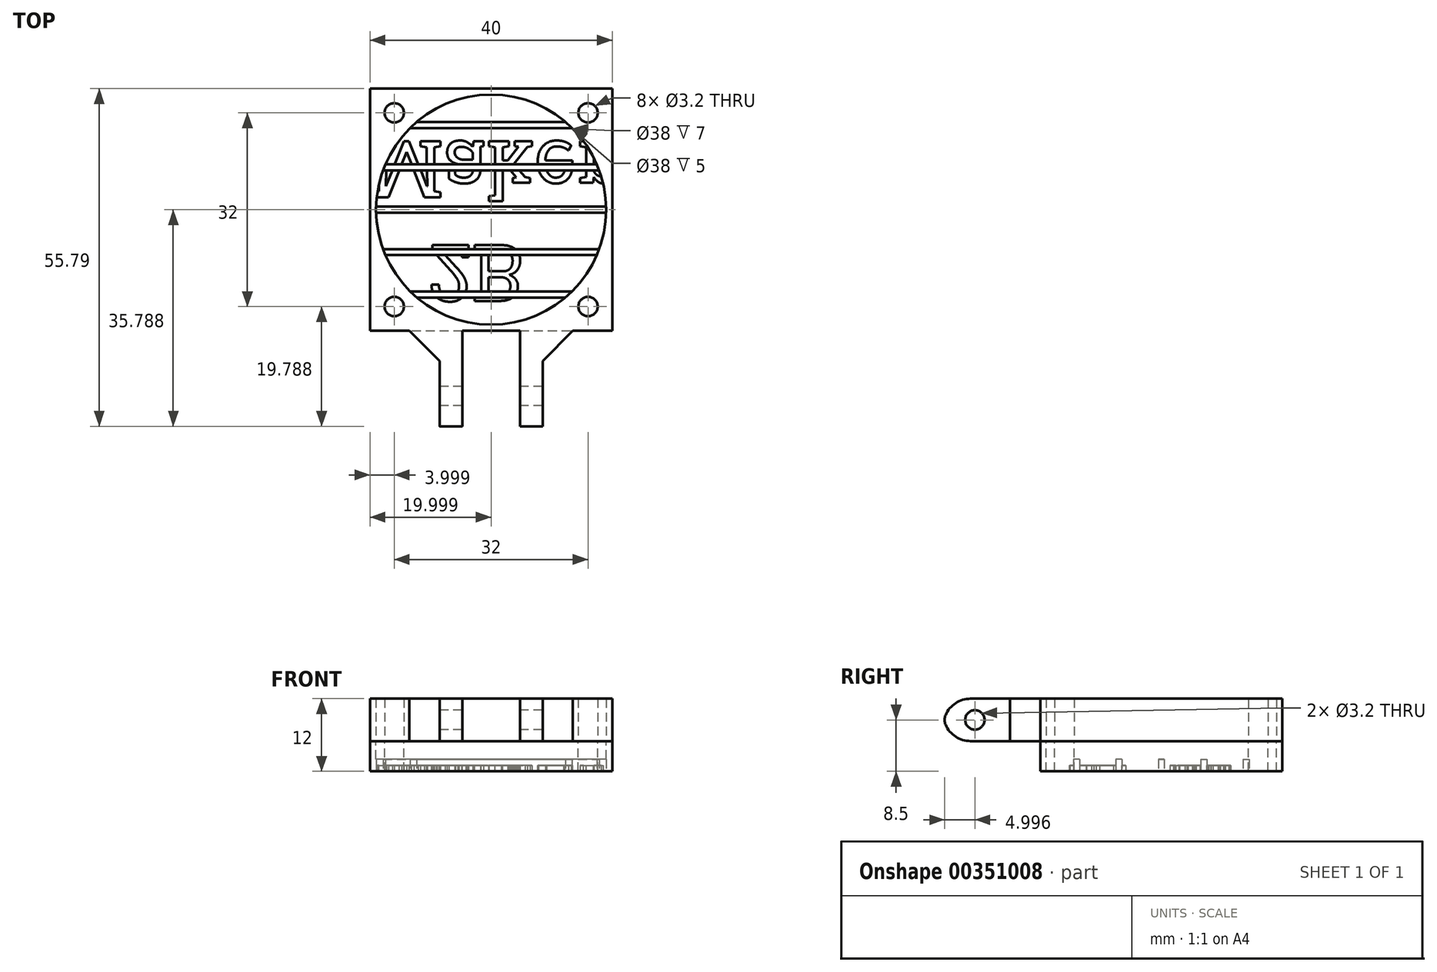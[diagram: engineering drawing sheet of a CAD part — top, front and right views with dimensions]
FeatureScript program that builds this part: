
annotation { "Feature Type Name" : "Feature", "Feature Type Description" : "" }
export const myFeature = defineFeature(function(context is Context, id is Id, definition is map)
    precondition{}
    {
        {
            var Q0;
            Q0=qCreatedBy(makeId("Top.planeOp"),FACE);
            var sketch = newSketch(context, id + "F0", { "sketchPlane" : qUnion([Q0])});
            skLineSegment(sketch, "E0.bottom", {"start": v(-56.17, -10.13) * mm, "end": v(-16.17, -10.13) * mm});
            skLineSegment(sketch, "E0.top", {"start": v(-56.17, 29.87) * mm, "end": v(-16.17, 29.87) * mm});
            skLineSegment(sketch, "E0.left", {"start": v(-56.17, -10.13) * mm, "end": v(-56.17, 29.87) * mm});
            skLineSegment(sketch, "E0.right", {"start": v(-16.17, -10.13) * mm, "end": v(-16.17, 29.87) * mm});
            skLineSegment(sketch, "E1.bottom", {"start": v(-55.17, 28.87) * mm, "end": v(-17.17, 28.87) * mm});
            skLineSegment(sketch, "E1.top", {"start": v(-55.17, -9.13) * mm, "end": v(-17.17, -9.13) * mm});
            skLineSegment(sketch, "E1.left", {"start": v(-55.17, 28.87) * mm, "end": v(-55.17, -9.13) * mm});
            skLineSegment(sketch, "E1.right", {"start": v(-17.17, 28.87) * mm, "end": v(-17.17, -9.13) * mm});
            skCircle(sketch, "E2", {"center": v(-52.17, 25.87) * mm, "radius": 1.6 * mm});
            skCircle(sketch, "E3", {"center": v(-52.17, -6.13) * mm, "radius": 1.6 * mm});
            skCircle(sketch, "E4", {"center": v(-20.17, -6.13) * mm, "radius": 1.6 * mm});
            skCircle(sketch, "E5", {"center": v(-20.17, 25.87) * mm, "radius": 1.6 * mm});
            skLineSegment(sketch, "E6", {"start": v(-56.17, 29.87) * mm, "end": v(-36.17, 29.87) * mm});
            skCircle(sketch, "E7", {"center": v(-36.17, 9.87) * mm, "radius": 19 * mm});
            skCircle(sketch, "E8", {"center": v(-36.17, 9.87) * mm, "radius": 18.03 * mm});
            skLineSegment(sketch, "E9", {"start": v(-52.3, 1.82) * mm, "end": v(-53.06, 1.15) * mm});
            skPoint(sketch, "E10.endSnap0", {"position": v(-36.17, -9.13) * mm});
            skLineSegment(sketch, "E11", {"start": v(-36.17, -10.1) * mm, "end": v(-31.82, -10.1) * mm});
            skLineSegment(sketch, "E12", {"start": v(-31.82, -10.1) * mm, "end": v(-28.07, -10.1) * mm});
            skLineSegment(sketch, "E13", {"start": v(-36.17, -10.1) * mm, "end": v(-40.52, -10.1) * mm});
            skLineSegment(sketch, "E14", {"start": v(-40.52, -10.1) * mm, "end": v(-44.27, -10.1) * mm});
            skSolve(sketch);
        }
        {
            var Q0;
            Q0 = qSketchRegion(id + "F0", true);
            var Q1;
            Q1=makeQuery(id+"F0.imprint","IMPRINT",FACE,{"disambiguationData":[TD([[makeQuery(id+"F0.imprint","IMPRINT",EDGE,{"derivedFrom":sQuery(id+"F0.wireOp",EDGE,"E2")}),-1.0]])]});
            var Q2;
            Q2=makeQuery(id+"F0.imprint","IMPRINT",FACE,{"disambiguationData":[TD([[makeQuery(id+"F0.imprint","IMPRINT",EDGE,{"derivedFrom":sQuery(id+"F0.wireOp",EDGE,"E5")}),-1.0]])]});
            var Q3;
            Q3=makeQuery(id+"F0.imprint","IMPRINT",FACE,{"disambiguationData":[TD([[makeQuery(id+"F0.imprint","IMPRINT",EDGE,{"derivedFrom":sQuery(id+"F0.wireOp",EDGE,"E3")}),-1.0]])]});
            var Q4;
            Q4=makeQuery(id+"F0.imprint","IMPRINT",FACE,{"disambiguationData":[TD([[makeQuery(id+"F0.imprint","IMPRINT",EDGE,{"derivedFrom":sQuery(id+"F0.wireOp",EDGE,"E4")}),-1.0]])]});
            extrude(context, id + "F1", {"entities" : qUnion([Q0, Q1, Q2, Q3, Q4]), "depth" : 7 * mm});
        }
        {
            var Q0;
            Q0=makeQuery(id+"F1.opExtrude","SWEPT_FACE",FACE,{"disambiguationData":[OSD([sQuery(id+"F0.wireOp",EDGE,"E0.bottom")])]});
            var sketch = newSketch(context, id + "F2", { "sketchPlane" : qUnion([Q0])});
            skLineSegment(sketch, "E15", {"start": v(-36.17, 0) * mm, "end": v(-36.17, 7) * mm});
            skLineSegment(sketch, "E16", {"start": v(-44.67, 7) * mm, "end": v(-44.67, 0) * mm});
            skLineSegment(sketch, "E17", {"start": v(-40.92, 7) * mm, "end": v(-40.92, 0) * mm});
            skLineSegment(sketch, "E18", {"start": v(-31.42, 0) * mm, "end": v(-31.42, 7) * mm});
            skLineSegment(sketch, "E19", {"start": v(-27.67, 0) * mm, "end": v(-27.67, 7) * mm});
            skSolve(sketch);
        }
        {
            var Q0;
            {var subQ0=sQuery(id+"F2.wireOp",EDGE,"E16");Q0=makeQuery(id+"F2.imprint","IMPRINT",FACE,{"disambiguationData":[TD([[makeQuery(id+"F2.imprint","IMPRINT",EDGE,{"derivedFrom":subQ0}),1.0]])]});}
            var Q1;
            {var subQ0=sQuery(id+"F2.wireOp",EDGE,"E18");Q1=makeQuery(id+"F2.imprint","IMPRINT",FACE,{"disambiguationData":[TD([[makeQuery(id+"F2.imprint","IMPRINT",EDGE,{"derivedFrom":subQ0}),-1.0]])]});}
            extrude(context, id + "F3", {"entities" : qUnion([Q0, Q1]), "operationType" : NewBodyOperationType.ADD, "depth" : 16 * mm});
        }
        {
            var Q0;
            {var subQ0=sQuery(id+"F0.wireOp",EDGE,"E0.bottom");var subQ1=makeQuery(id+"F1.opExtrude","CAP_EDGE",EDGE,{"disambiguationData":[OSD([subQ0])],"isStart":false});Q0=makeQuery(id+"F3.opExtrude","CAP_EDGE",EDGE,{"disambiguationData":[OSD([subQ0]),TDD([makeQuery(id+"F2.imprint","IMPRINT",EDGE,{"disambiguationData":[TD([[makeQuery(id+"F2.imprint","INTERSECT",VERTEX,{"derivedFrom":[subQ1,sQuery(id+"F2.wireOp",EDGE,"E18")]}),-1.0]])],"derivedFrom":subQ1})])],"isStart":false});}
            var Q1;
            {var subQ0=sQuery(id+"F0.wireOp",EDGE,"E0.bottom");var subQ1=makeQuery(id+"F1.opExtrude","CAP_EDGE",EDGE,{"disambiguationData":[OSD([subQ0])],"isStart":false});Q1=makeQuery(id+"F3.opExtrude","CAP_EDGE",EDGE,{"disambiguationData":[OSD([subQ0]),TDD([makeQuery(id+"F2.imprint","IMPRINT",EDGE,{"disambiguationData":[TD([[makeQuery(id+"F2.imprint","INTERSECT",VERTEX,{"derivedFrom":[subQ1,sQuery(id+"F2.wireOp",EDGE,"E16")]}),-1.0]])],"derivedFrom":subQ1})])],"isStart":false});}
            var Q2;
            {var subQ0=sQuery(id+"F0.wireOp",EDGE,"E0.bottom");var subQ1=makeQuery(id+"F1.opExtrude","CAP_EDGE",EDGE,{"disambiguationData":[OSD([subQ0])],"isStart":true});Q2=makeQuery(id+"F3.opExtrude","CAP_EDGE",EDGE,{"disambiguationData":[OSD([subQ0]),TDD([makeQuery(id+"F2.imprint","IMPRINT",EDGE,{"disambiguationData":[TD([[makeQuery(id+"F2.imprint","INTERSECT",VERTEX,{"derivedFrom":[subQ1,sQuery(id+"F2.wireOp",EDGE,"E16")]}),-1.0]])],"derivedFrom":subQ1})])],"isStart":false});}
            var Q3;
            {var subQ0=sQuery(id+"F0.wireOp",EDGE,"E0.bottom");var subQ1=makeQuery(id+"F1.opExtrude","CAP_EDGE",EDGE,{"disambiguationData":[OSD([subQ0])],"isStart":true});Q3=makeQuery(id+"F3.opExtrude","CAP_EDGE",EDGE,{"disambiguationData":[OSD([subQ0]),TDD([makeQuery(id+"F2.imprint","IMPRINT",EDGE,{"disambiguationData":[TD([[makeQuery(id+"F2.imprint","INTERSECT",VERTEX,{"derivedFrom":[subQ1,sQuery(id+"F2.wireOp",EDGE,"E18")]}),-1.0]])],"derivedFrom":subQ1})])],"isStart":false});}
            fillet(context, id + "F4", {"entities" : qUnion([Q0, Q1, Q2, Q3]), "radius" : 4.5 * mm, "tangentPropagation" : true, "allowEdgeOverflow" : false});
        }
        {
            var Q0;
            {var subQ0=sQuery(id+"F2.wireOp",EDGE,"E16");var subQ1=sQuery(id+"F0.wireOp",EDGE,"E0.bottom");var subQ2=makeQuery(id+"F1.opExtrude","CAP_EDGE",EDGE,{"disambiguationData":[OSD([subQ1])],"isStart":false});var subQ4=makeQuery(id+"F1.opExtrude","CAP_EDGE",EDGE,{"disambiguationData":[OSD([subQ1])],"isStart":true});Q0=makeQuery(id+"F4.opFillet","BLEND_EDGE",EDGE,{"blendedFrom":[makeQuery(id+"F3.opExtrude","CAP_EDGE",EDGE,{"disambiguationData":[OSD([subQ1]),TDD([makeQuery(id+"F2.imprint","IMPRINT",EDGE,{"disambiguationData":[TD([[makeQuery(id+"F2.imprint","INTERSECT",VERTEX,{"derivedFrom":[subQ4,subQ0]}),-1.0]])],"derivedFrom":subQ4})])],"isStart":false}),makeQuery(id+"F3.opExtrude","CAP_EDGE",EDGE,{"disambiguationData":[OSD([subQ1]),TDD([makeQuery(id+"F2.imprint","IMPRINT",EDGE,{"disambiguationData":[TD([[makeQuery(id+"F2.imprint","INTERSECT",VERTEX,{"derivedFrom":[subQ2,subQ0]}),-1.0]])],"derivedFrom":subQ2})])],"isStart":false})],"blendedInto":[]});}
            var Q1;
            {var subQ0=sQuery(id+"F2.wireOp",EDGE,"E18");var subQ1=sQuery(id+"F0.wireOp",EDGE,"E0.bottom");var subQ2=makeQuery(id+"F1.opExtrude","CAP_EDGE",EDGE,{"disambiguationData":[OSD([subQ1])],"isStart":false});var subQ4=makeQuery(id+"F1.opExtrude","CAP_EDGE",EDGE,{"disambiguationData":[OSD([subQ1])],"isStart":true});Q1=makeQuery(id+"F4.opFillet","BLEND_EDGE",EDGE,{"blendedFrom":[makeQuery(id+"F3.opExtrude","CAP_EDGE",EDGE,{"disambiguationData":[OSD([subQ1]),TDD([makeQuery(id+"F2.imprint","IMPRINT",EDGE,{"disambiguationData":[TD([[makeQuery(id+"F2.imprint","INTERSECT",VERTEX,{"derivedFrom":[subQ4,subQ0]}),-1.0]])],"derivedFrom":subQ4})])],"isStart":false}),makeQuery(id+"F3.opExtrude","CAP_EDGE",EDGE,{"disambiguationData":[OSD([subQ1]),TDD([makeQuery(id+"F2.imprint","IMPRINT",EDGE,{"disambiguationData":[TD([[makeQuery(id+"F2.imprint","INTERSECT",VERTEX,{"derivedFrom":[subQ2,subQ0]}),-1.0]])],"derivedFrom":subQ2})])],"isStart":false})],"blendedInto":[]});}
            fillet(context, id + "F5", {"entities" : qUnion([Q0, Q1]), "radius" : 2 * mm, "tangentPropagation" : true, "allowEdgeOverflow" : false});
        }
        {
            var Q0;
            Q0=makeQuery(id+"F3.opExtrude","SWEPT_FACE",FACE,{"disambiguationData":[OSD([sQuery(id+"F2.wireOp",EDGE,"E16")])]});
            var sketch = newSketch(context, id + "F6", { "sketchPlane" : qUnion([Q0])});
            skLineSegment(sketch, "E20", {"start": v(25.92, 3.5) * mm, "end": v(20.92, 3.5) * mm});
            skPoint(sketch, "E20.endSnap0", {"position": v(25.92, 3.5) * mm});
            skCircle(sketch, "E21", {"center": v(20.92, 3.5) * mm, "radius": 1.6 * mm});
            skSolve(sketch);
        }
        {
            var Q0;
            Q0=makeQuery(id+"F6.imprint","IMPRINT",FACE,{"disambiguationData":[TD([[makeQuery(id+"F6.imprint","IMPRINT",EDGE,{"derivedFrom":sQuery(id+"F6.wireOp",EDGE,"E21")}),1.0]])]});
            extrude(context, id + "F7", {"entities" : qUnion([Q0]), "operationType" : NewBodyOperationType.REMOVE, "oppositeDirection" : true, "depth" : 17 * mm});
        }
        {
            var Q0;
            Q0=makeQuery(id+"F3.opExtrude","CAP_EDGE",EDGE,{"disambiguationData":[OSD([sQuery(id+"F2.wireOp",EDGE,"E19")])],"isStart":true});
            var Q1;
            Q1=makeQuery(id+"F3.opExtrude","CAP_EDGE",EDGE,{"disambiguationData":[OSD([sQuery(id+"F2.wireOp",EDGE,"E16")])],"isStart":true});
            chamfer(context, id + "F8", {"entities" : qUnion([Q0, Q1]), "width" : 5 * mm, "tangentPropagation" : true});
        }
        {
            var Q0;
            Q0 = qSketchRegion(id + "F0", true);
            var Q1;
            Q1=makeQuery(id+"F0.imprint","IMPRINT",FACE,{"disambiguationData":[TD([[makeQuery(id+"F0.imprint","IMPRINT",EDGE,{"derivedFrom":sQuery(id+"F0.wireOp",EDGE,"E4")}),-1.0]])]});
            var Q2;
            Q2=makeQuery(id+"F0.imprint","IMPRINT",FACE,{"disambiguationData":[TD([[makeQuery(id+"F0.imprint","IMPRINT",EDGE,{"derivedFrom":sQuery(id+"F0.wireOp",EDGE,"E5")}),-1.0]])]});
            var Q3;
            Q3=makeQuery(id+"F0.imprint","IMPRINT",FACE,{"disambiguationData":[TD([[makeQuery(id+"F0.imprint","IMPRINT",EDGE,{"derivedFrom":sQuery(id+"F0.wireOp",EDGE,"E2")}),-1.0]])]});
            var Q4;
            Q4=makeQuery(id+"F0.imprint","IMPRINT",FACE,{"disambiguationData":[TD([[makeQuery(id+"F0.imprint","IMPRINT",EDGE,{"derivedFrom":sQuery(id+"F0.wireOp",EDGE,"E3")}),-1.0]])]});
            extrude(context, id + "F9", {"entities" : qUnion([Q0, Q1, Q2, Q3, Q4]), "oppositeDirection" : true, "depth" : 5 * mm});
        }
        {
            var Q0;
            Q0=makeQuery(id+"F9.opExtrude","CAP_FACE",FACE,{"disambiguationData":[OSD([sQuery(id+"F0.wireOp",EDGE,"E0.bottom"),sQuery(id+"F0.wireOp",EDGE,"E0.top"),sQuery(id+"F0.wireOp",EDGE,"E0.left"),sQuery(id+"F0.wireOp",EDGE,"E0.right"),sQuery(id+"F0.wireOp",EDGE,"E2"),sQuery(id+"F0.wireOp",EDGE,"E3"),sQuery(id+"F0.wireOp",EDGE,"E4"),sQuery(id+"F0.wireOp",EDGE,"E5"),sQuery(id+"F0.wireOp",EDGE,"E6"),sQuery(id+"F0.wireOp",EDGE,"E7")])],"isStart":false});
            var sketch = newSketch(context, id + "F10", { "sketchPlane" : qUnion([Q0])});
            skLineSegment(sketch, "E22", {"start": v(-48.45, -24.37) * mm, "end": v(-23.9, -24.37) * mm});
            skLineSegment(sketch, "E23", {"start": v(-22.8, -23.37) * mm, "end": v(-49.54, -23.37) * mm});
            skLineSegment(sketch, "E24", {"start": v(-38.06, -17.37) * mm, "end": v(-18.71, -17.37) * mm});
            skLineSegment(sketch, "E25", {"start": v(-18.71, -17.37) * mm, "end": v(-53.63, -17.37) * mm});
            skLineSegment(sketch, "E26", {"start": v(-54.02, -16.37) * mm, "end": v(-18.32, -16.37) * mm});
            skLineSegment(sketch, "E27", {"start": v(-17.18, -10.37) * mm, "end": v(-55.16, -10.37) * mm});
            skLineSegment(sketch, "E28", {"start": v(-55.16, -9.37) * mm, "end": v(-17.18, -9.37) * mm});
            skLineSegment(sketch, "E29", {"start": v(-18.32, -3.37) * mm, "end": v(-54.02, -3.37) * mm});
            skLineSegment(sketch, "E30", {"start": v(-18.71, -2.37) * mm, "end": v(-53.63, -2.37) * mm});
            skLineSegment(sketch, "E31", {"start": v(-49.54, 3.63) * mm, "end": v(-22.8, 3.63) * mm});
            skLineSegment(sketch, "E32", {"start": v(-48.45, 4.63) * mm, "end": v(-23.9, 4.63) * mm});
            skSolve(sketch);
        }
        {
            var Q0;
            Q0 = qSketchRegion(id + "F10", true);
            var Q1;
            {var subQ0=sQuery(id+"F10.wireOp",EDGE,"E31");Q1=makeQuery(id+"F10.imprint","IMPRINT",FACE,{"disambiguationData":[TD([[makeQuery(id+"F10.imprint","IMPRINT",EDGE,{"derivedFrom":subQ0}),1.0]])]});}
            var Q2;
            {var subQ0=sQuery(id+"F10.wireOp",EDGE,"E29");Q2=makeQuery(id+"F10.imprint","IMPRINT",FACE,{"disambiguationData":[TD([[makeQuery(id+"F10.imprint","IMPRINT",EDGE,{"derivedFrom":subQ0}),-1.0]])]});}
            var Q3;
            {var subQ0=sQuery(id+"F10.wireOp",EDGE,"E27");Q3=makeQuery(id+"F10.imprint","IMPRINT",FACE,{"disambiguationData":[TD([[makeQuery(id+"F10.imprint","IMPRINT",EDGE,{"derivedFrom":subQ0}),-1.0]])]});}
            var Q4;
            {var subQ3=sQuery(id+"F10.wireOp",EDGE,"E26");Q4=makeQuery(id+"F10.imprint","IMPRINT",FACE,{"disambiguationData":[TD([[makeQuery(id+"F10.imprint","IMPRINT",EDGE,{"derivedFrom":subQ3}),-1.0]])]});}
            var Q5;
            {var subQ0=sQuery(id+"F10.wireOp",EDGE,"E22");Q5=makeQuery(id+"F10.imprint","IMPRINT",FACE,{"disambiguationData":[TD([[makeQuery(id+"F10.imprint","IMPRINT",EDGE,{"derivedFrom":subQ0}),1.0]])]});}
            extrude(context, id + "F11", {"entities" : qUnion([Q0, Q1, Q2, Q3, Q4, Q5]), "operationType" : NewBodyOperationType.ADD, "oppositeDirection" : true, "depth" : 2 * mm});
        }
        {
            var Q0;
            {var subQ0=sQuery(id+"F0.wireOp",EDGE,"E7");Q0=makeQuery(id+"F11.boolean.opBoolean","MERGE",FACE,{"derivedFrom":[makeQuery(id+"F9.opExtrude","CAP_FACE",FACE,{"disambiguationData":[OSD([sQuery(id+"F0.wireOp",EDGE,"E0.bottom"),sQuery(id+"F0.wireOp",EDGE,"E0.top"),sQuery(id+"F0.wireOp",EDGE,"E0.left"),sQuery(id+"F0.wireOp",EDGE,"E0.right"),sQuery(id+"F0.wireOp",EDGE,"E2"),sQuery(id+"F0.wireOp",EDGE,"E3"),sQuery(id+"F0.wireOp",EDGE,"E4"),sQuery(id+"F0.wireOp",EDGE,"E5"),sQuery(id+"F0.wireOp",EDGE,"E6"),subQ0])],"isStart":false}),makeQuery(id+"F11.opExtrude","CAP_FACE",FACE,{"disambiguationData":[OSD([subQ0,sQuery(id+"F10.wireOp",EDGE,"E22"),sQuery(id+"F10.wireOp",EDGE,"E23")])],"isStart":true}),makeQuery(id+"F11.opExtrude","CAP_FACE",FACE,{"disambiguationData":[OSD([subQ0,sQuery(id+"F10.wireOp",EDGE,"E25"),sQuery(id+"F10.wireOp",EDGE,"E26")])],"isStart":true}),makeQuery(id+"F11.opExtrude","CAP_FACE",FACE,{"disambiguationData":[OSD([subQ0,sQuery(id+"F10.wireOp",EDGE,"E27"),sQuery(id+"F10.wireOp",EDGE,"E28")])],"isStart":true}),makeQuery(id+"F11.opExtrude","CAP_FACE",FACE,{"disambiguationData":[OSD([subQ0,sQuery(id+"F10.wireOp",EDGE,"E29"),sQuery(id+"F10.wireOp",EDGE,"E30")])],"isStart":true}),makeQuery(id+"F11.opExtrude","CAP_FACE",FACE,{"disambiguationData":[OSD([subQ0,sQuery(id+"F10.wireOp",EDGE,"E31"),sQuery(id+"F10.wireOp",EDGE,"E32")])],"isStart":true})]});}
            var sketch = newSketch(context, id + "F12", { "sketchPlane" : qUnion([Q0])});
            skText(sketch, "E33", { "text": "   2B \nMaker", "fontName": "RobotoSlab-Regular.ttf"});
            const initialGuessF12  = {"E33": [-0.05617, -0.00402, 1, 0, 0.00935]};
            skSetInitialGuess(sketch, initialGuessF12);
            skSolve(sketch);
        }
        {
            var Q0;
            Q0 = qSketchRegion(id + "F12", true);
            extrude(context, id + "F13", {"entities" : qUnion([Q0]), "operationType" : NewBodyOperationType.ADD, "oppositeDirection" : true, "depth" : 1 * mm});
        }
    });
